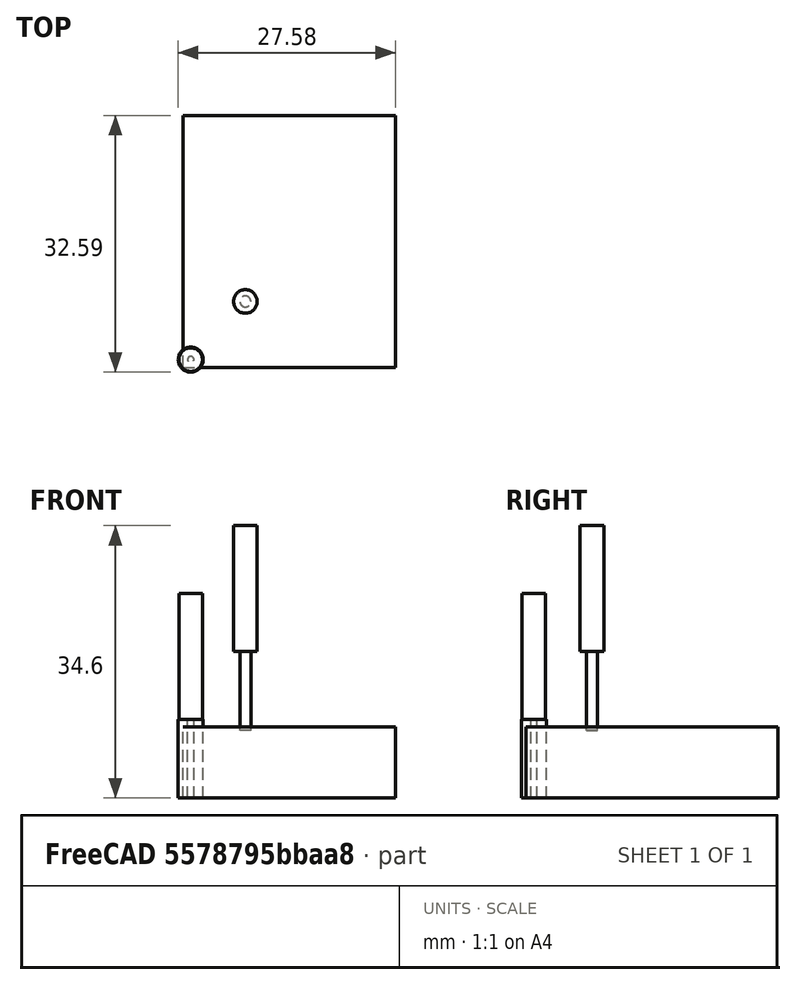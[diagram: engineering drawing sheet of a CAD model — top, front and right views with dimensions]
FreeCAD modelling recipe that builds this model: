
FCSTD DOCUMENT  (FreeCAD 0.22R35966 (Git))
Label: test
License: All rights reserved
LicenseURL: http://en.wikipedia.org/wiki/All_rights_reserved
objects: Part::FeaturePython×6, Path::FeaturePython×5, App::DocumentObjectGroup×3, PartDesign::AdditiveBox×1, PartDesign::Body×1, Part::Part2DObjectPython×1, Part::Extrusion×1, Part::Cut×1, App::FeaturePython×1, Mesh::FeaturePython×1
note: 13 computed .brp shape members not serialized (recipe doc carries the construction recipe); baked Part::Feature solids carry a one-line shape summary decoded from their .brp

FEATURE [PartDesign::AdditiveBox] Box
  AttacherType = Attacher::AttachEngine3D
  Height = 9
  Length = 25
  MapMode = 5
  Support = -> [XY_Plane]
  Suppressed = false
  Width = 30
FEATURE [PartDesign::Body] Body
  Group = -> [Box]
  Origin = -> Origin
  Tip = -> Box
FEATURE [Part::Part2DObjectPython] ShapeString  # Draft 2D object (typed FeaturePython)
  FontFile = /Library/Fonts/Arial Unicode.ttf
  Fuse = false
  Justification = 6
  JustificationReference = 0
  KeepLeftMargin = false
  MakeFace = true
  ObliqueAngle = 0
  Placement = pos=(5,5,9.1) rot=(0,0,1;0rad)
  ScaleToSize = true
  Size = 20
  String = B
  Tracking = 0
FEATURE [Part::Extrusion] Extrude
  Base = -> ShapeString
  Dir = (0,0,1)
  DirMode = 2
  FaceMakerClass = Part::FaceMakerBullseye
  LengthFwd = 0.01
  LengthRev = 0
  Reversed = true
  Solid = true
  Symmetric = false
FEATURE [Part::Cut] Cut
  Base = -> Body
  Tool = -> Extrude
FEATURE [App::FeaturePython] SetupSheet  # Path/CAM operation (typed FeaturePython)
  ClearanceHeightExpression = OpStockZMax+SetupSheet.ClearanceHeightOffset
  ClearanceHeightOffset = 5
  CoolantMode = 0
  CoolantModes = None | Flood | Mist
  FinalDepthExpression = OpFinalDepth
  HorizRapid = 0
  SafeHeightExpression = OpStockZMax+SetupSheet.SafeHeightOffset
  SafeHeightOffset = 3
  StartDepthExpression = OpStartDepth
  StepDownExpression = OpToolDiameter
  VertRapid = 0
FEATURE [Part::FeaturePython] Clone  label="Model-Cut"  # Draft clone (typed FeaturePython)
  AttacherType = Attacher::AttachEngine3D
  Fuse = false
  Objects = -> [Cut]
  PathResource = Model
  Scale = (1,1,1)
FEATURE [App::DocumentObjectGroup] Model
  Group = -> [Clone]
FEATURE [Part::FeaturePython] ToolBit  label="0.8mm-endmill"  # Path/CAM toolbit (typed FeaturePython)
  BitPropertyNames = Chipload | CuttingEdgeHeight | Diameter | Flutes | Length | Material | ShankDiameter | SpindleDirection
  BitShape = /Applications/FreeCAD.app/Contents/Resources/Mod/Path/Tools/Shape/endmill.fcstd
  Chipload = 0
  CuttingEdgeHeight = 10
  Diameter = 0.8
  Flutes = 0
  Length = 26
  Material = 0
  ShankDiameter = 3
  ShapeName = endmill
  SpindleDirection = 0
FEATURE [Path::FeaturePython] __8mm_endmill  label="0.8mm-endmill001"  # Path/CAM operation (typed FeaturePython)
  HorizFeed = 16.6667
  HorizRapid = 0
  SpindleDir = 0
  SpindleSpeed = 10000
  Tool = -> ToolBit
  ToolNumber = 3
  VertFeed = 16.6667
  VertRapid = 0
  expr: HorizRapid = SetupSheet.HorizRapid
  expr: VertRapid = SetupSheet.VertRapid
FEATURE [Part::FeaturePython] ToolBit001  label="1.4mm-endmill"  # Path/CAM toolbit (typed FeaturePython)
  BitPropertyNames = Chipload | CuttingEdgeHeight | Diameter | Flutes | Length | Material | ShankDiameter | SpindleDirection
  BitShape = /Applications/FreeCAD.app/Contents/Resources/Mod/Path/Tools/Shape/endmill.fcstd
  Chipload = 0
  CuttingEdgeHeight = 10
  Diameter = 1.4
  Flutes = 0
  Length = 26
  Material = 0
  ShankDiameter = 3
  ShapeName = endmill
  SpindleDirection = 0
FEATURE [Path::FeaturePython] __4mm_endmill  label="1.4mm-endmill001"  # Path/CAM operation (typed FeaturePython)
  HorizFeed = 16.6667
  HorizRapid = 0
  SpindleDir = 0
  SpindleSpeed = 10000
  Tool = -> ToolBit001
  ToolNumber = 2
  VertFeed = 16.6667
  VertRapid = 0
  expr: HorizRapid = SetupSheet.HorizRapid
  expr: VertRapid = SetupSheet.VertRapid
FEATURE [Part::FeaturePython] ToolBit002  label="3.175mm-endmill"  # Path/CAM toolbit (typed FeaturePython)
  BitPropertyNames = Chipload | CuttingEdgeHeight | Diameter | Flutes | Length | Material | ShankDiameter | SpindleDirection
  BitShape = /Applications/FreeCAD.app/Contents/Resources/Mod/Path/Tools/Shape/endmill.fcstd
  Chipload = 0
  CuttingEdgeHeight = 10
  Diameter = 3.17
  Flutes = 0
  Length = 26
  Material = 0
  ShankDiameter = 3
  ShapeName = endmill
  SpindleDirection = 0
FEATURE [Path::FeaturePython] __175mm_endmill  label="3.175mm-endmill001"  # Path/CAM operation (typed FeaturePython)
  HorizFeed = 4.16667
  HorizRapid = 0
  SpindleDir = 0
  SpindleSpeed = 1000
  Tool = -> ToolBit002
  ToolNumber = 4
  VertFeed = 4.16667
  VertRapid = 0
  expr: HorizRapid = SetupSheet.HorizRapid
  expr: VertRapid = SetupSheet.VertRapid
FEATURE [App::DocumentObjectGroup] Tools
  Group = -> [__8mm_endmill,__4mm_endmill,__175mm_endmill]
FEATURE [Part::FeaturePython] Stock  # WARN: FeaturePython — macro-defined, semantics opaque (R4)
  Base = -> Model
  ExtXneg = 1
  ExtXpos = 1
  ExtYneg = 1
  ExtYpos = 1
  ExtZneg = 0
  ExtZpos = 0
  StockType = FromBase
FEATURE [Part::FeaturePython] CutTool  # WARN: FeaturePython — macro-defined, semantics opaque (R4)
  Placement = pos=(6.94353,7.38372,8.6) rot=(0,0,1;0rad)
FEATURE [Path::FeaturePython] MillFace  # Path/CAM operation (typed FeaturePython)
  Active = true
  AreaParams:
    Tolerance = 1e-07
    FitArcs = True
    Simplify = False
    CleanDistance = 0.0
    Accuracy = 0.01
    Unit = 1.0
    MinArcPoints = 4
    MaxArcPoints = 100
    ClipperScale = 10000000.0
    Fill = 0
    Coplanar = 0
    Reorient = True
    Outline = False
    Explode = False
    OpenMode = 0
    Deflection = 0.01
    SubjectFill = 0
    ClipFill = 0
    Offset = 0.0
    ExtraPass = 0
    Stepover = 0.0
    LastStepover = 0.0
    JoinType = 0
    EndType = 0
    MiterLimit = 2.0
    RoundPrecision = 0.0
    PocketMode = 4
    ToolRadius = 1.585
    PocketExtraOffset = 0.0
    PocketStepover = 1.585
    PocketLastStepover = 0.0
    FromCenter = True
    Angle = 45.0
    AngleShift = 0.0
    Shift = 0.0
    Thicken = False
    SectionCount = -1
    Stepdown = 1.0
    SectionOffset = 0.0
    SectionTolerance = 1e-06
    SectionMode = 2
    Project = False
  Base = -> [Clone]
  BoundaryShape = 0
  ClearEdges = false
  ClearanceHeight = 14
  CoolantMode = 0
  CutMode = 0
  CycleTime = 00:02:26
  ExcludeRaisedAreas = false
  ExtraOffset = 0
  FinalDepth = 8.2
  FinishDepth = 0
  KeepToolDown = false
  MinTravel = false
  OffsetPattern = 2
  OpFinalDepth = 9
  OpStartDepth = 12.17
  OpStockZMax = 9
  OpStockZMin = 0
  OpToolDiameter = 3.17
  PathParams = {'orientation': 1, 'feedrate': 4.166666666666667, 'feedrate_v': 4.166666666666667, 'verbose': True, 'resume_height': 12.0, 'retraction': 14.0, 'return_end': True, 'preamble': False}
  PocketLastStepOver = 0
  SafeHeight = 12
  SplitArcs = false
  StartAt = 0
  StartDepth = 8.4
  StartPoint = (0,0,0)
  StepDown = 3.17
  StepOver = 50
  ToolController = -> __175mm_endmill
  UseRestMachining = false
  UseStartPoint = false
  ZigZagAngle = 45
  expr: ClearanceHeight = OpStockZMax + SetupSheet.ClearanceHeightOffset
  expr: FinalDepth = 8.2
  expr: SafeHeight = OpStockZMax + SetupSheet.SafeHeightOffset
  expr: StartDepth = 8.4
  expr: StepDown = OpToolDiameter
FEATURE [App::DocumentObjectGroup] Operations
  Group = -> [MillFace]
FEATURE [Path::FeaturePython] Job  # Path/CAM operation (typed FeaturePython)
  CycleTime = 00:02:26
  Fixtures = G54
  GeometryTolerance = 0.01
  JobType = 0
  LastPostProcessDate = 2024-02-16 15:34:00.418519
  LastPostProcessOutput = /Volumes/NEW VOLUME/cleanup.nc
  Model = -> Model
  Operations = -> Operations
  OrderOutputBy = 0
  PostProcessor = 1
  PostProcessorOutputFile = <userpath>/3d_projects/CNC-stuff/placard/nameplate.nc
  SetupSheet = -> SetupSheet
  SplitOutput = false
  Stock = -> Stock
  Tools = -> Tools
FEATURE [Mesh::FeaturePython] CutMaterial  # WARN: FeaturePython — macro-defined, semantics opaque (R4)
